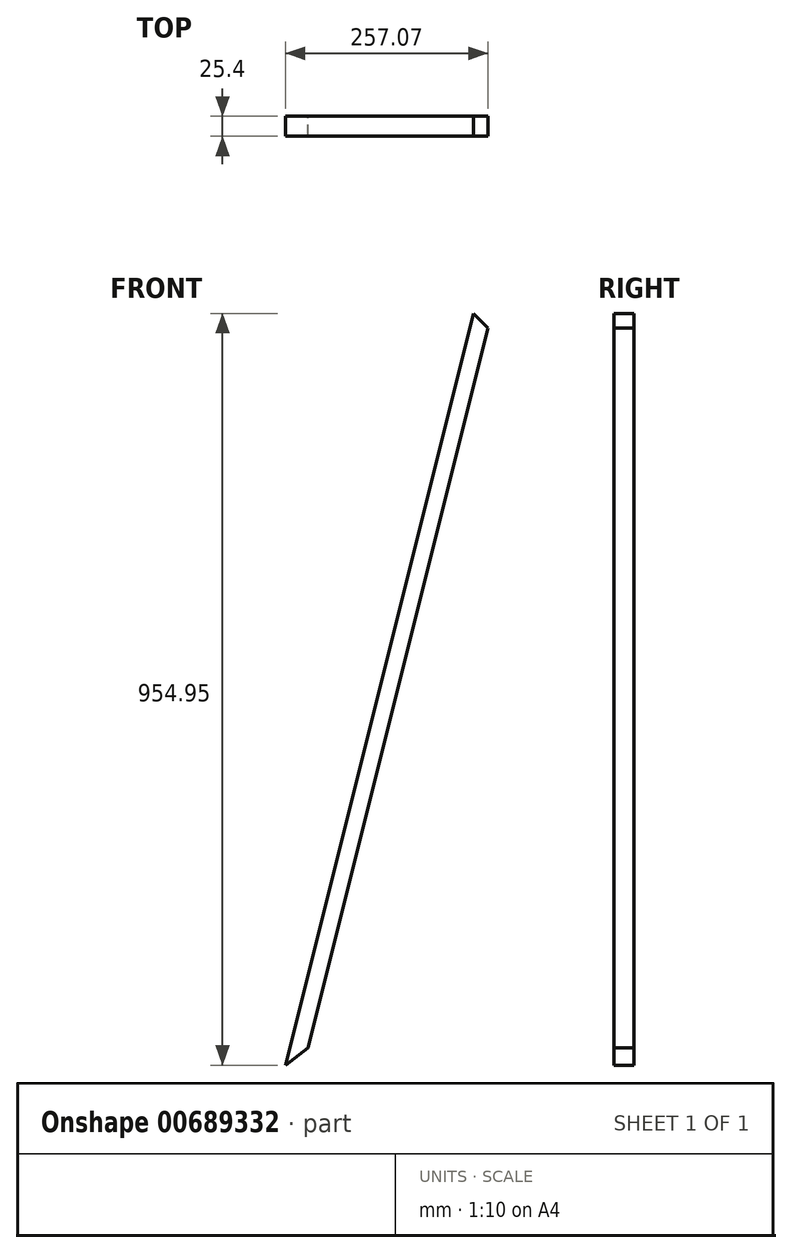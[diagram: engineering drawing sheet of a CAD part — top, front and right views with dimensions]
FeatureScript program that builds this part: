
annotation { "Feature Type Name" : "Feature", "Feature Type Description" : "" }
export const myFeature = defineFeature(function(context is Context, id is Id, definition is map)
    precondition{}
    {
        {
            var Q0;
            Q0=qCreatedBy(makeId("Front.planeOp"),FACE);
            var sketch = newSketch(context, id + "F0", { "sketchPlane" : qUnion([Q0])});
            skLineSegment(sketch, "E0", {"start": v(228.6, -42.72) * mm, "end": v(0, 871.68) * mm});
            skLineSegment(sketch, "E1", {"start": v(0, 871.68) * mm, "end": v(-228.6, -42.72) * mm});
            skLineSegment(sketch, "E2", {"start": v(-228.6, -42.72) * mm, "end": v(228.6, -42.72) * mm});
            skLineSegment(sketch, "E3.0", {"start": v(257.07, -64.94) * mm, "end": v(18.33, 890.01) * mm});
            skLineSegment(sketch, "E4.0", {"start": v(-18.33, 890.01) * mm, "end": v(-257.07, -64.94) * mm});
            skLineSegment(sketch, "E5.0", {"start": v(-257.07, -64.94) * mm, "end": v(257.07, -64.94) * mm});
            skLineSegment(sketch, "E6", {"start": v(0, 871.68) * mm, "end": v(18.33, 890.01) * mm});
            skLineSegment(sketch, "E7", {"start": v(-18.33, 890.01) * mm, "end": v(0, 871.68) * mm});
            skLineSegment(sketch, "E8", {"start": v(-228.6, -42.72) * mm, "end": v(-257.07, -64.94) * mm});
            skLineSegment(sketch, "E9", {"start": v(228.6, -42.72) * mm, "end": v(257.07, -64.94) * mm});
            skLineSegment(sketch, "E10", {"start": v(0, 871.68) * mm, "end": v(0, -42.72) * mm});
            skSolve(sketch);
        }
        {
            var Q0;
            Q0=makeQuery(id+"F0.imprint","IMPRINT",FACE,{"disambiguationData":[TD([[makeQuery(id+"F0.imprint","IMPRINT",EDGE,{"derivedFrom":sQuery(id+"F0.wireOp",EDGE,"E1")}),-1.0]])]});
            extrude(context, id + "F1", {"entities" : qUnion([Q0]), "depth" : 25.4 * mm, "offsetDistance" : 25.4 * mm});
        }
    });
